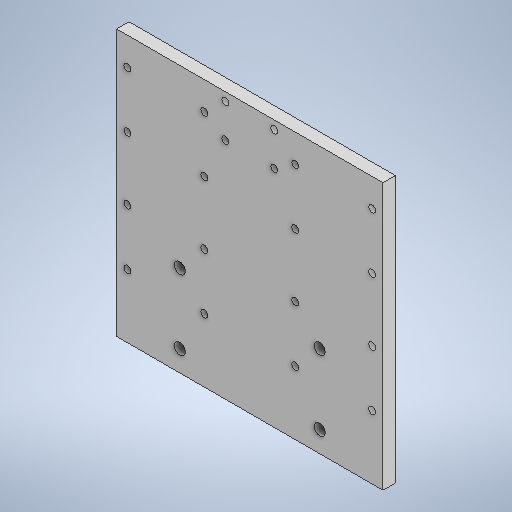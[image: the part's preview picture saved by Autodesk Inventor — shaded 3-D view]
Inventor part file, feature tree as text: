
AUTODESK INVENTOR PART (.ipt)
format: ipt  version: 2025.2 (Build 292293000, 293)  size: 267,264 bytes
history: native  units: mm
features: extrude x4
ambient origin geometry x8: Origin, YZ Plane, XZ Plane, XY Plane, X Axis, Y Axis, Z Axis, Center Point
bodies: Solid1 (feature_tree)
feature tree (4):
  extrude  "Extrusion1"  Depth=190.5mm
  extrude  "Extrusion2"  Depth=190.5mm
  extrude  "Extrusion3"  Depth=8.89mm TaperAngle=0.0deg
  extrude  "Extrusion4"  Depth=100.0mm
